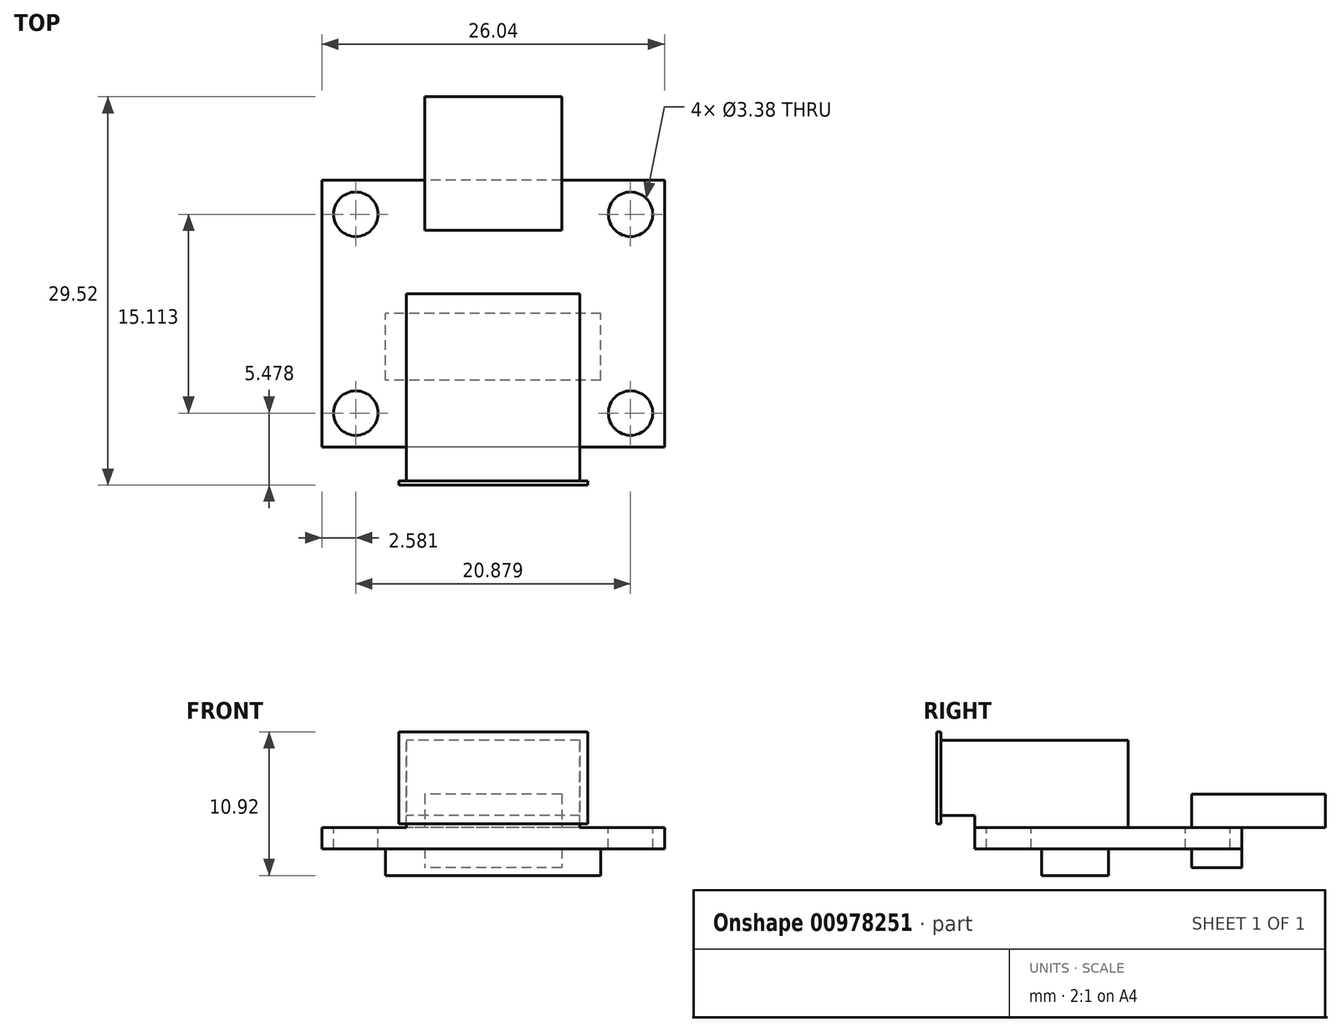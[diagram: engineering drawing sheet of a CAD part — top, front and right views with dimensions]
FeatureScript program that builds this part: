
annotation { "Feature Type Name" : "Feature", "Feature Type Description" : "" }
export const myFeature = defineFeature(function(context is Context, id is Id, definition is map)
    precondition{}
    {
        {
            var Q0;
            Q0=qCreatedBy(makeId("Right.planeOp"),FACE);
            var sketch = newSketch(context, id + "F0", { "sketchPlane" : qUnion([Q0])});
            skLineSegment(sketch, "E0.bottom", {"start": v(0, 0) * mm, "end": v(20.27, 0) * mm});
            skLineSegment(sketch, "E0.top", {"start": v(0, -1.6) * mm, "end": v(20.27, -1.6) * mm});
            skLineSegment(sketch, "E0.left", {"start": v(0, 0) * mm, "end": v(0, -1.6) * mm});
            skLineSegment(sketch, "E0.right", {"start": v(20.27, 0) * mm, "end": v(20.27, -1.6) * mm});
            skLineSegment(sketch, "E1", {"start": v(20.27, 0) * mm, "end": v(11.63, 0) * mm});
            skLineSegment(sketch, "E2.bottom", {"start": v(11.63, 0) * mm, "end": v(-2.9, 0) * mm});
            skLineSegment(sketch, "E2.top", {"start": v(11.63, 6.63) * mm, "end": v(-2.9, 6.63) * mm});
            skLineSegment(sketch, "E2.left", {"start": v(11.63, 0) * mm, "end": v(11.63, 6.63) * mm});
            skLineSegment(sketch, "E2.right", {"start": v(-2.9, 0) * mm, "end": v(-2.9, 6.63) * mm});
            skLineSegment(sketch, "E3", {"start": v(0, -1.6) * mm, "end": v(10.16, -1.6) * mm});
            skLineSegment(sketch, "E4.bottom", {"start": v(5.08, -1.6) * mm, "end": v(10.16, -1.6) * mm});
            skLineSegment(sketch, "E4.top", {"start": v(5.08, -3.63) * mm, "end": v(10.16, -3.63) * mm});
            skLineSegment(sketch, "E4.left", {"start": v(5.08, -1.6) * mm, "end": v(5.08, -3.63) * mm});
            skLineSegment(sketch, "E4.right", {"start": v(10.16, -1.6) * mm, "end": v(10.16, -3.63) * mm});
            skLineSegment(sketch, "E5", {"start": v(20.27, 0) * mm, "end": v(20.27, 2.54) * mm});
            skLineSegment(sketch, "E6.bottom", {"start": v(20.27, 2.54) * mm, "end": v(16.46, 2.54) * mm});
            skLineSegment(sketch, "E6.top", {"start": v(20.27, 0) * mm, "end": v(16.46, 0) * mm});
            skLineSegment(sketch, "E6.left", {"start": v(20.27, 2.54) * mm, "end": v(20.27, 0) * mm});
            skLineSegment(sketch, "E6.right", {"start": v(16.46, 2.54) * mm, "end": v(16.46, 0) * mm});
            skLineSegment(sketch, "E7.bottom", {"start": v(16.46, 2.54) * mm, "end": v(20.27, 2.54) * mm});
            skLineSegment(sketch, "E7.top", {"start": v(16.46, -3.05) * mm, "end": v(20.27, -3.05) * mm});
            skLineSegment(sketch, "E7.left", {"start": v(16.46, 2.54) * mm, "end": v(16.46, -3.05) * mm});
            skLineSegment(sketch, "E7.right", {"start": v(20.27, 2.54) * mm, "end": v(20.27, -3.05) * mm});
            skLineSegment(sketch, "E8.bottom", {"start": v(16.46, 2.54) * mm, "end": v(26.62, 2.54) * mm});
            skLineSegment(sketch, "E8.top", {"start": v(16.46, 0) * mm, "end": v(26.62, 0) * mm});
            skLineSegment(sketch, "E8.right", {"start": v(26.62, 2.54) * mm, "end": v(26.62, 0) * mm});
            skLineSegment(sketch, "E9.bottom", {"start": v(-2.9, 6.63) * mm, "end": v(11.63, 6.63) * mm});
            skLineSegment(sketch, "E9.top", {"start": v(-2.9, 0.94) * mm, "end": v(11.63, 0.94) * mm});
            skLineSegment(sketch, "E9.left", {"start": v(-2.9, 6.63) * mm, "end": v(-2.9, 0.94) * mm});
            skLineSegment(sketch, "E9.right", {"start": v(11.63, 6.63) * mm, "end": v(11.63, 0.94) * mm});
            skLineSegment(sketch, "E10", {"start": v(0, 0) * mm, "end": v(0, 0.94) * mm});
            skLineSegment(sketch, "E11", {"start": v(-2.9, 3.78) * mm, "end": v(-2.6, 3.78) * mm});
            skLineSegment(sketch, "E12.bottom", {"start": v(-2.9, 7.29) * mm, "end": v(-2.6, 7.29) * mm});
            skLineSegment(sketch, "E12.top", {"start": v(-2.9, 0.28) * mm, "end": v(-2.6, 0.28) * mm});
            skLineSegment(sketch, "E12.left", {"start": v(-2.9, 7.29) * mm, "end": v(-2.9, 0.28) * mm});
            skLineSegment(sketch, "E12.right", {"start": v(-2.6, 7.29) * mm, "end": v(-2.6, 0.28) * mm});
            skPoint(sketch, "E12.middle", {"position": v(-2.74, 3.78) * mm});
            skSolve(sketch);
        }
        {
            var Q0;
            {var subQ0=sQuery(id+"F0.wireOp",EDGE,"E0.left");Q0=makeQuery(id+"F0.imprint","IMPRINT",FACE,{"disambiguationData":[TD([[makeQuery(id+"F0.imprint","IMPRINT",EDGE,{"derivedFrom":subQ0}),1.0]])]});}
            var Q1;
            {var subQ0=sQuery(id+"F0.wireOp",EDGE,"E0.right");Q1=makeQuery(id+"F0.imprint","IMPRINT",FACE,{"disambiguationData":[TD([[makeQuery(id+"F0.imprint","IMPRINT",EDGE,{"derivedFrom":subQ0}),-1.0]])]});}
            extrude(context, id + "F1", {"entities" : qUnion([Q0, Q1]), "endBound" : BoundingType.SYMMETRIC, "depth" : 26.03 * mm, "offsetDistance" : 25.4 * mm});
        }
        {
            var Q0;
            {var subQ0=sQuery(id+"F0.wireOp",EDGE,"E10");Q0=makeQuery(id+"F0.imprint","IMPRINT",FACE,{"disambiguationData":[TD([[makeQuery(id+"F0.imprint","IMPRINT",EDGE,{"derivedFrom":subQ0}),-1.0]])]});}
            var Q1;
            {var subQ1=sQuery(id+"F0.wireOp",EDGE,"E2.left");var subQ6=sQuery(id+"F0.wireOp",EDGE,"E2.top");var subQ7=makeQuery(id+"F0.imprint","INTERSECT",VERTEX,{"derivedFrom":[subQ6,subQ1]});Q1=makeQuery(id+"F0.imprint","IMPRINT",FACE,{"disambiguationData":[TD([[makeQuery(id+"F0.imprint","IMPRINT",EDGE,{"disambiguationData":[TD([[subQ7,-1.0]])],"derivedFrom":subQ6}),1.0]])]});}
            extrude(context, id + "F2", {"entities" : qUnion([Q0, Q1]), "operationType" : NewBodyOperationType.ADD, "endBound" : BoundingType.SYMMETRIC, "depth" : 13.18 * mm, "offsetDistance" : 25.4 * mm});
        }
        {
            var Q0;
            {var subQ5=sQuery(id+"F0.wireOp",EDGE,"E11");Q0=makeQuery(id+"F0.imprint","IMPRINT",FACE,{"disambiguationData":[TD([[makeQuery(id+"F0.imprint","IMPRINT",EDGE,{"derivedFrom":subQ5}),1.0]])]});}
            var Q1;
            {var subQ4=sQuery(id+"F0.wireOp",EDGE,"E12.bottom");Q1=makeQuery(id+"F0.imprint","IMPRINT",FACE,{"disambiguationData":[TD([[makeQuery(id+"F0.imprint","IMPRINT",EDGE,{"derivedFrom":subQ4}),-1.0]])]});}
            var Q2;
            {var subQ0=sQuery(id+"F0.wireOp",EDGE,"E11");Q2=makeQuery(id+"F0.imprint","IMPRINT",FACE,{"disambiguationData":[TD([[makeQuery(id+"F0.imprint","IMPRINT",EDGE,{"derivedFrom":subQ0}),-1.0]])]});}
            var Q3;
            {var subQ0=sQuery(id+"F0.wireOp",EDGE,"E12.top");Q3=makeQuery(id+"F0.imprint","IMPRINT",FACE,{"disambiguationData":[TD([[makeQuery(id+"F0.imprint","IMPRINT",EDGE,{"derivedFrom":subQ0}),1.0]])]});}
            extrude(context, id + "F3", {"entities" : qUnion([Q0, Q1, Q2, Q3]), "operationType" : NewBodyOperationType.ADD, "endBound" : BoundingType.SYMMETRIC, "depth" : 14.35 * mm, "offsetDistance" : 25.4 * mm});
        }
        {
            var Q0;
            {var subQ0=sQuery(id+"F0.wireOp",EDGE,"E5");Q0=makeQuery(id+"F0.imprint","IMPRINT",FACE,{"disambiguationData":[TD([[makeQuery(id+"F0.imprint","IMPRINT",EDGE,{"derivedFrom":subQ0}),1.0]])]});}
            var Q1;
            Q1=makeQuery(id+"F0.imprint","IMPRINT",FACE,{"disambiguationData":[TD([[makeQuery(id+"F0.imprint","IMPRINT",EDGE,{"derivedFrom":sQuery(id+"F0.wireOp",EDGE,"E5")}),-1.0]])]});
            var Q2;
            {var subQ4=sQuery(id+"F0.wireOp",EDGE,"E7.top");Q2=makeQuery(id+"F0.imprint","IMPRINT",FACE,{"disambiguationData":[TD([[makeQuery(id+"F0.imprint","IMPRINT",EDGE,{"derivedFrom":subQ4}),1.0]])]});}
            extrude(context, id + "F4", {"entities" : qUnion([Q0, Q1, Q2]), "operationType" : NewBodyOperationType.ADD, "endBound" : BoundingType.SYMMETRIC, "depth" : 10.4 * mm, "offsetDistance" : 25.4 * mm});
        }
        {
            var Q0;
            Q0=makeQuery(id+"F0.imprint","IMPRINT",FACE,{"disambiguationData":[TD([[makeQuery(id+"F0.imprint","IMPRINT",EDGE,{"derivedFrom":sQuery(id+"F0.wireOp",EDGE,"E4.top")}),1.0]])]});
            extrude(context, id + "F5", {"entities" : qUnion([Q0]), "operationType" : NewBodyOperationType.ADD, "endBound" : BoundingType.SYMMETRIC, "depth" : 16.36 * mm, "offsetDistance" : 25.4 * mm});
        }
        {
            var Q0;
            Q0=makeQuery(id+"F1.opExtrude","SWEPT_FACE",FACE,{"disambiguationData":[OSD([sQuery(id+"F0.wireOp",EDGE,"E0.bottom")])]});
            var sketch = newSketch(context, id + "F6", { "sketchPlane" : qUnion([Q0])});
            skLineSegment(sketch, "E13.bottom", {"start": v(-13.02, 0) * mm, "end": v(-12.13, 0) * mm});
            skLineSegment(sketch, "E13.top", {"start": v(-13.02, 0.89) * mm, "end": v(-12.13, 0.89) * mm});
            skLineSegment(sketch, "E13.left", {"start": v(-13.02, 0) * mm, "end": v(-13.02, 0.89) * mm});
            skLineSegment(sketch, "E13.right", {"start": v(-12.13, 0) * mm, "end": v(-12.13, 0.89) * mm});
            skLineSegment(sketch, "E14.bottom", {"start": v(-13.02, 20.27) * mm, "end": v(-12.13, 20.27) * mm});
            skLineSegment(sketch, "E14.top", {"start": v(-13.02, 19.38) * mm, "end": v(-12.13, 19.38) * mm});
            skLineSegment(sketch, "E14.left", {"start": v(-13.02, 20.27) * mm, "end": v(-13.02, 19.38) * mm});
            skLineSegment(sketch, "E14.right", {"start": v(-12.13, 20.27) * mm, "end": v(-12.13, 19.38) * mm});
            skLineSegment(sketch, "E15.bottom", {"start": v(13.02, 0) * mm, "end": v(12.13, 0) * mm});
            skLineSegment(sketch, "E15.top", {"start": v(13.02, 0.89) * mm, "end": v(12.13, 0.89) * mm});
            skLineSegment(sketch, "E15.left", {"start": v(13.02, 0) * mm, "end": v(13.02, 0.89) * mm});
            skLineSegment(sketch, "E15.right", {"start": v(12.13, 0) * mm, "end": v(12.13, 0.89) * mm});
            skLineSegment(sketch, "E16.bottom", {"start": v(13.02, 20.27) * mm, "end": v(12.13, 20.27) * mm});
            skLineSegment(sketch, "E16.top", {"start": v(13.02, 19.38) * mm, "end": v(12.13, 19.38) * mm});
            skLineSegment(sketch, "E16.left", {"start": v(13.02, 20.27) * mm, "end": v(13.02, 19.38) * mm});
            skLineSegment(sketch, "E16.right", {"start": v(12.13, 20.27) * mm, "end": v(12.13, 19.38) * mm});
            skLineSegment(sketch, "E17.bottom", {"start": v(12.13, 0.89) * mm, "end": v(8.75, 0.89) * mm});
            skLineSegment(sketch, "E17.top", {"start": v(12.13, 4.27) * mm, "end": v(8.75, 4.27) * mm});
            skLineSegment(sketch, "E17.left", {"start": v(12.13, 0.89) * mm, "end": v(12.13, 4.27) * mm});
            skLineSegment(sketch, "E17.right", {"start": v(8.75, 0.89) * mm, "end": v(8.75, 4.27) * mm});
            skLineSegment(sketch, "E18.bottom", {"start": v(-12.13, 0.89) * mm, "end": v(-8.75, 0.89) * mm});
            skLineSegment(sketch, "E18.top", {"start": v(-12.13, 4.27) * mm, "end": v(-8.75, 4.27) * mm});
            skLineSegment(sketch, "E18.left", {"start": v(-12.13, 0.89) * mm, "end": v(-12.13, 4.27) * mm});
            skLineSegment(sketch, "E18.right", {"start": v(-8.75, 0.89) * mm, "end": v(-8.75, 4.27) * mm});
            skLineSegment(sketch, "E19.bottom", {"start": v(-12.13, 19.38) * mm, "end": v(-8.75, 19.38) * mm});
            skLineSegment(sketch, "E19.top", {"start": v(-12.13, 16) * mm, "end": v(-8.75, 16) * mm});
            skLineSegment(sketch, "E19.left", {"start": v(-12.13, 19.38) * mm, "end": v(-12.13, 16) * mm});
            skLineSegment(sketch, "E19.right", {"start": v(-8.75, 19.38) * mm, "end": v(-8.75, 16) * mm});
            skLineSegment(sketch, "E20.bottom", {"start": v(12.13, 19.38) * mm, "end": v(8.75, 19.38) * mm});
            skLineSegment(sketch, "E20.top", {"start": v(12.13, 16) * mm, "end": v(8.75, 16) * mm});
            skLineSegment(sketch, "E20.left", {"start": v(12.13, 19.38) * mm, "end": v(12.13, 16) * mm});
            skLineSegment(sketch, "E20.right", {"start": v(8.75, 19.38) * mm, "end": v(8.75, 16) * mm});
            skLineSegment(sketch, "E21", {"start": v(10.44, 0.89) * mm, "end": v(10.44, 4.27) * mm});
            skLineSegment(sketch, "E22", {"start": v(10.44, 4.27) * mm, "end": v(10.44, 16) * mm});
            skLineSegment(sketch, "E23", {"start": v(10.44, 16) * mm, "end": v(10.44, 19.38) * mm});
            skLineSegment(sketch, "E24", {"start": v(-10.44, 0.89) * mm, "end": v(-10.44, 4.27) * mm});
            skLineSegment(sketch, "E25", {"start": v(-10.44, 4.27) * mm, "end": v(-10.44, 16) * mm});
            skLineSegment(sketch, "E26", {"start": v(-10.44, 16) * mm, "end": v(-10.44, 19.38) * mm});
            skCircle(sketch, "E27", {"center": v(-10.44, 2.58) * mm, "radius": 1.69 * mm});
            skCircle(sketch, "E28", {"center": v(-10.44, 17.7) * mm, "radius": 1.69 * mm});
            skCircle(sketch, "E29", {"center": v(10.44, 2.58) * mm, "radius": 1.69 * mm});
            skCircle(sketch, "E30", {"center": v(10.44, 17.7) * mm, "radius": 1.69 * mm});
            skSolve(sketch);
        }
        {
            var Q0;
            {var subQ0=sQuery(id+"F6.wireOp",EDGE,"E24");Q0=makeQuery(id+"F6.imprint","IMPRINT",FACE,{"disambiguationData":[TD([[makeQuery(id+"F6.imprint","IMPRINT",EDGE,{"derivedFrom":subQ0}),-1.0]])]});}
            var Q1;
            {var subQ0=sQuery(id+"F6.wireOp",EDGE,"E24");Q1=makeQuery(id+"F6.imprint","IMPRINT",FACE,{"disambiguationData":[TD([[makeQuery(id+"F6.imprint","IMPRINT",EDGE,{"derivedFrom":subQ0}),1.0]])]});}
            var Q2;
            {var subQ0=sQuery(id+"F6.wireOp",EDGE,"E26");Q2=makeQuery(id+"F6.imprint","IMPRINT",FACE,{"disambiguationData":[TD([[makeQuery(id+"F6.imprint","IMPRINT",EDGE,{"derivedFrom":subQ0}),-1.0]])]});}
            var Q3;
            {var subQ0=sQuery(id+"F6.wireOp",EDGE,"E26");Q3=makeQuery(id+"F6.imprint","IMPRINT",FACE,{"disambiguationData":[TD([[makeQuery(id+"F6.imprint","IMPRINT",EDGE,{"derivedFrom":subQ0}),1.0]])]});}
            var Q4;
            {var subQ0=sQuery(id+"F6.wireOp",EDGE,"E23");Q4=makeQuery(id+"F6.imprint","IMPRINT",FACE,{"disambiguationData":[TD([[makeQuery(id+"F6.imprint","IMPRINT",EDGE,{"derivedFrom":subQ0}),1.0]])]});}
            var Q5;
            {var subQ0=sQuery(id+"F6.wireOp",EDGE,"E23");Q5=makeQuery(id+"F6.imprint","IMPRINT",FACE,{"disambiguationData":[TD([[makeQuery(id+"F6.imprint","IMPRINT",EDGE,{"derivedFrom":subQ0}),-1.0]])]});}
            var Q6;
            {var subQ0=sQuery(id+"F6.wireOp",EDGE,"E21");Q6=makeQuery(id+"F6.imprint","IMPRINT",FACE,{"disambiguationData":[TD([[makeQuery(id+"F6.imprint","IMPRINT",EDGE,{"derivedFrom":subQ0}),1.0]])]});}
            var Q7;
            {var subQ0=sQuery(id+"F6.wireOp",EDGE,"E21");Q7=makeQuery(id+"F6.imprint","IMPRINT",FACE,{"disambiguationData":[TD([[makeQuery(id+"F6.imprint","IMPRINT",EDGE,{"derivedFrom":subQ0}),-1.0]])]});}
            extrude(context, id + "F7", {"entities" : qUnion([Q0, Q1, Q2, Q3, Q4, Q5, Q6, Q7]), "operationType" : NewBodyOperationType.REMOVE, "endBound" : BoundingType.THROUGH_ALL, "oppositeDirection" : true, "depth" : 25.4 * mm, "offsetDistance" : 25.4 * mm});
        }
    });
